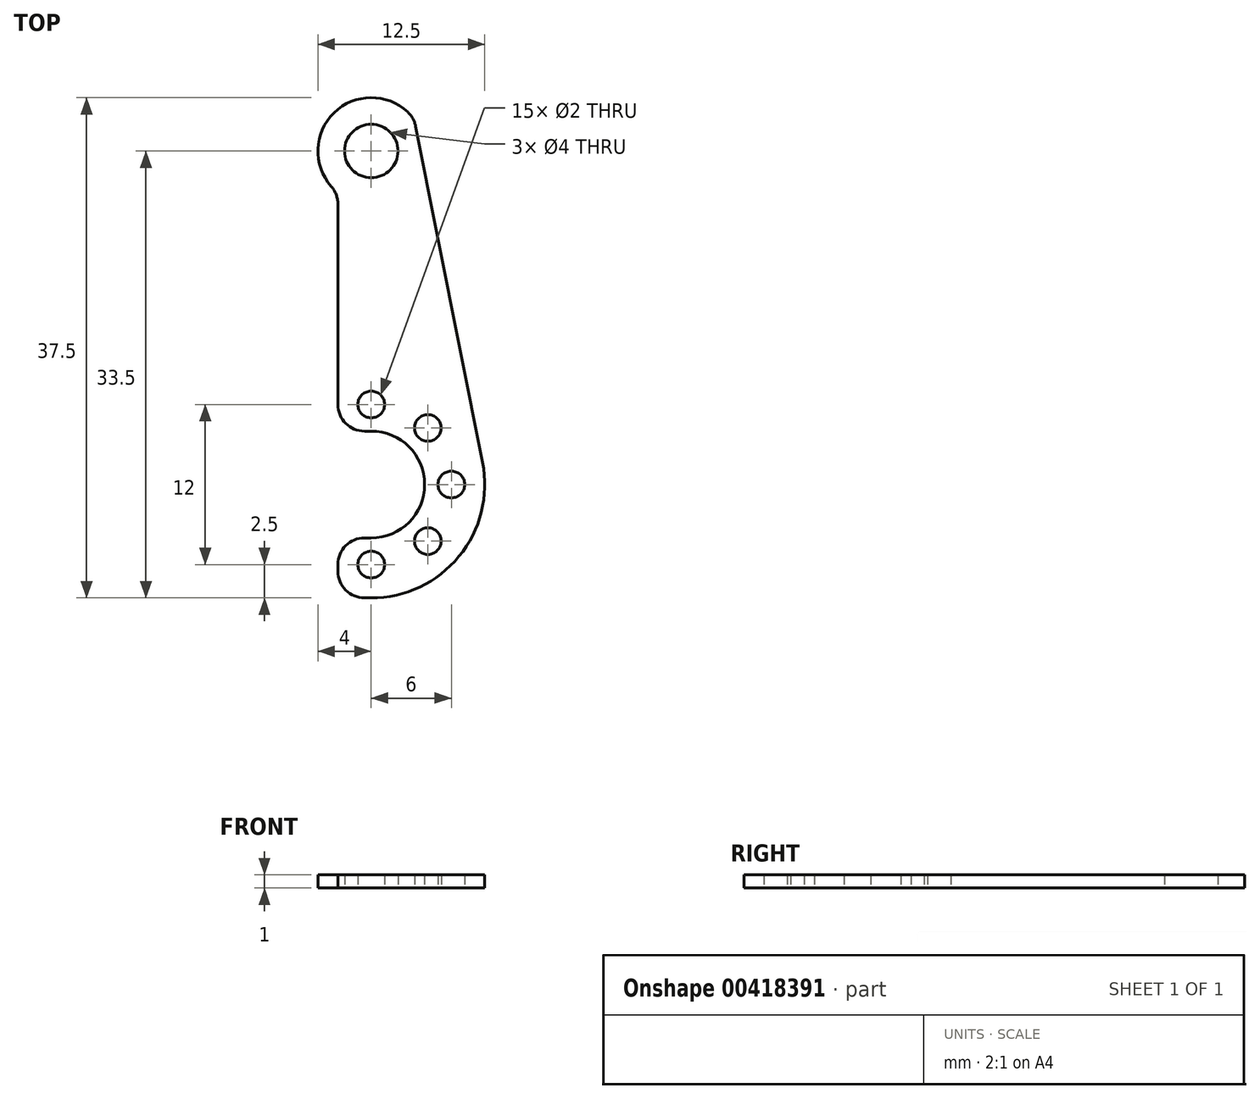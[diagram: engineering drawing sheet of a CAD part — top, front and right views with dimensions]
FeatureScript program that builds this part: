
annotation { "Feature Type Name" : "Feature", "Feature Type Description" : "" }
export const myFeature = defineFeature(function(context is Context, id is Id, definition is map)
    precondition{}
    {
        {
            var Q0;
            Q0=qCreatedBy(makeId("Top.planeOp"),FACE);
            var sketch = newSketch(context, id + "F0", { "sketchPlane" : qUnion([Q0])});
            skArc(sketch, "E0", {"start": v(0, -4) * mm, "mid": v(4, 0) * mm, "end": v(0, 4) * mm});
            skCircle(sketch, "E1", {"center": v(0, 25) * mm, "radius": 2 * mm});
            skCircle(sketch, "E2", {"center": v(0, 6) * mm, "radius": 1 * mm});
            skCircle(sketch, "E3.4.0", {"center": v(0, -6) * mm, "radius": 1 * mm});
            skCircle(sketch, "E3.5.0", {"center": v(4.24, -4.24) * mm, "radius": 1 * mm});
            skCircle(sketch, "E3.6.0", {"center": v(6, 0) * mm, "radius": 1 * mm});
            skCircle(sketch, "E3.7.0", {"center": v(4.24, 4.24) * mm, "radius": 1 * mm});
            skLineSegment(sketch, "E4", {"start": v(0, 4) * mm, "end": v(-2.5, 4) * mm});
            skLineSegment(sketch, "E5", {"start": v(-2.5, 4) * mm, "end": v(-2.5, 28.5) * mm});
            skLineSegment(sketch, "E6", {"start": v(-2.5, 28.5) * mm, "end": v(3, 28.5) * mm});
            skLineSegment(sketch, "E7", {"start": v(3, 28.5) * mm, "end": v(8.34, 1.66) * mm});
            skArc(sketch, "E8", {"start": v(-2.5, -8.12) * mm, "mid": v(5.7, -6.3) * mm, "end": v(8.34, 1.66) * mm});
            skPoint(sketch, "E9.orphan", {"position": v(8.67, 0) * mm});
            skLineSegment(sketch, "E10", {"start": v(0, -4) * mm, "end": v(-2.5, -4) * mm});
            skLineSegment(sketch, "E11", {"start": v(-2.5, -4) * mm, "end": v(-2.5, -8.12) * mm});
            skLineSegment(sketch, "E12", {"start": v(0, -6) * mm, "end": v(-2.5, -6) * mm, "construction": true});
            skLineSegment(sketch, "E13", {"start": v(0, -8.5) * mm, "end": v(-2.5, -8.5) * mm});
            skLineSegment(sketch, "E14", {"start": v(-2.5, -8.5) * mm, "end": v(-2.5, -8.12) * mm});
            skCircle(sketch, "E15", {"center": v(0, 25) * mm, "radius": 4 * mm});
            skSolve(sketch);
        }
        {
            var Q0;
            {var subQ0=sQuery(id+"F0.wireOp",EDGE,"E15");var subQ1=sQuery(id+"F0.wireOp",EDGE,"E5");var subQ2=makeQuery(id+"F0.imprint","INTERSECT",VERTEX,{"disambiguationData":[OD(0.0)],"derivedFrom":[subQ1,subQ0]});Q0=makeQuery(id+"F0.imprint","IMPRINT",FACE,{"disambiguationData":[TD([[makeQuery(id+"F0.imprint","IMPRINT",EDGE,{"disambiguationData":[TD([[subQ2,-1.0]])],"derivedFrom":subQ1}),1.0]])]});}
            var Q1;
            {var subQ0=sQuery(id+"F0.wireOp",EDGE,"E15");var subQ1=sQuery(id+"F0.wireOp",EDGE,"E6");var subQ2=makeQuery(id+"F0.imprint","INTERSECT",VERTEX,{"disambiguationData":[OD(0.0)],"derivedFrom":[subQ1,subQ0]});Q1=makeQuery(id+"F0.imprint","IMPRINT",FACE,{"disambiguationData":[TD([[makeQuery(id+"F0.imprint","IMPRINT",EDGE,{"disambiguationData":[TD([[subQ2,-1.0]])],"derivedFrom":subQ1}),1.0]])]});}
            var Q2;
            {var subQ0=sQuery(id+"F0.wireOp",EDGE,"E15");var subQ1=sQuery(id+"F0.wireOp",EDGE,"E7");var subQ2=makeQuery(id+"F0.imprint","INTERSECT",VERTEX,{"disambiguationData":[OD(0.0)],"derivedFrom":[subQ1,subQ0]});Q2=makeQuery(id+"F0.imprint","IMPRINT",FACE,{"disambiguationData":[TD([[makeQuery(id+"F0.imprint","IMPRINT",EDGE,{"disambiguationData":[TD([[subQ2,-1.0]])],"derivedFrom":subQ1}),1.0]])]});}
            var Q3;
            {var subQ2=sQuery(id+"F0.wireOp",EDGE,"E13");Q3=makeQuery(id+"F0.imprint","IMPRINT",FACE,{"disambiguationData":[TD([[makeQuery(id+"F0.imprint","IMPRINT",EDGE,{"derivedFrom":subQ2}),-1.0]])]});}
            var Q4;
            Q4=makeQuery(id+"F0.imprint","IMPRINT",FACE,{"disambiguationData":[TD([[makeQuery(id+"F0.imprint","IMPRINT",EDGE,{"derivedFrom":sQuery(id+"F0.wireOp",EDGE,"E0")}),-1.0]])]});
            var Q5;
            Q5=makeQuery(id+"F0.imprint","IMPRINT",FACE,{"disambiguationData":[TD([[makeQuery(id+"F0.imprint","IMPRINT",EDGE,{"derivedFrom":sQuery(id+"F0.wireOp",EDGE,"E1")}),-1.0]])]});
            extrude(context, id + "F1", {"entities" : qUnion([Q0, Q1, Q2, Q3, Q4, Q5]), "depth" : 1 * mm});
        }
        {
            var Q0;
            Q0=makeQuery(id+"F1.opExtrude","SWEPT_EDGE",EDGE,{"disambiguationData":[OSD([sQuery(id+"F0.wireOp",EDGE,"E4"),sQuery(id+"F0.wireOp",EDGE,"E5")])]});
            var Q1;
            Q1=makeQuery(id+"F1.opExtrude","SWEPT_EDGE",EDGE,{"disambiguationData":[OSD([sQuery(id+"F0.wireOp",EDGE,"E10"),sQuery(id+"F0.wireOp",EDGE,"E11")])]});
            var Q2;
            Q2=makeQuery(id+"F1.opExtrude","SWEPT_EDGE",EDGE,{"disambiguationData":[OSD([sQuery(id+"F0.wireOp",EDGE,"E13"),sQuery(id+"F0.wireOp",EDGE,"E14")])]});
            var Q3;
            Q3=makeQuery(id+"F1.opExtrude","SWEPT_EDGE",EDGE,{"disambiguationData":[OSD([sQuery(id+"F0.wireOp",EDGE,"E6"),sQuery(id+"F0.wireOp",EDGE,"E7")])]});
            var Q4;
            Q4=makeQuery(id+"F1.opExtrude","SWEPT_EDGE",EDGE,{"disambiguationData":[OSD([sQuery(id+"F0.wireOp",EDGE,"E5"),sQuery(id+"F0.wireOp",EDGE,"E6")])]});
            fillet(context, id + "F2", {"entities" : qUnion([Q0, Q1, Q2, Q3, Q4]), "radius" : 2 * mm, "tangentPropagation" : true, "allowEdgeOverflow" : false});
        }
    });
